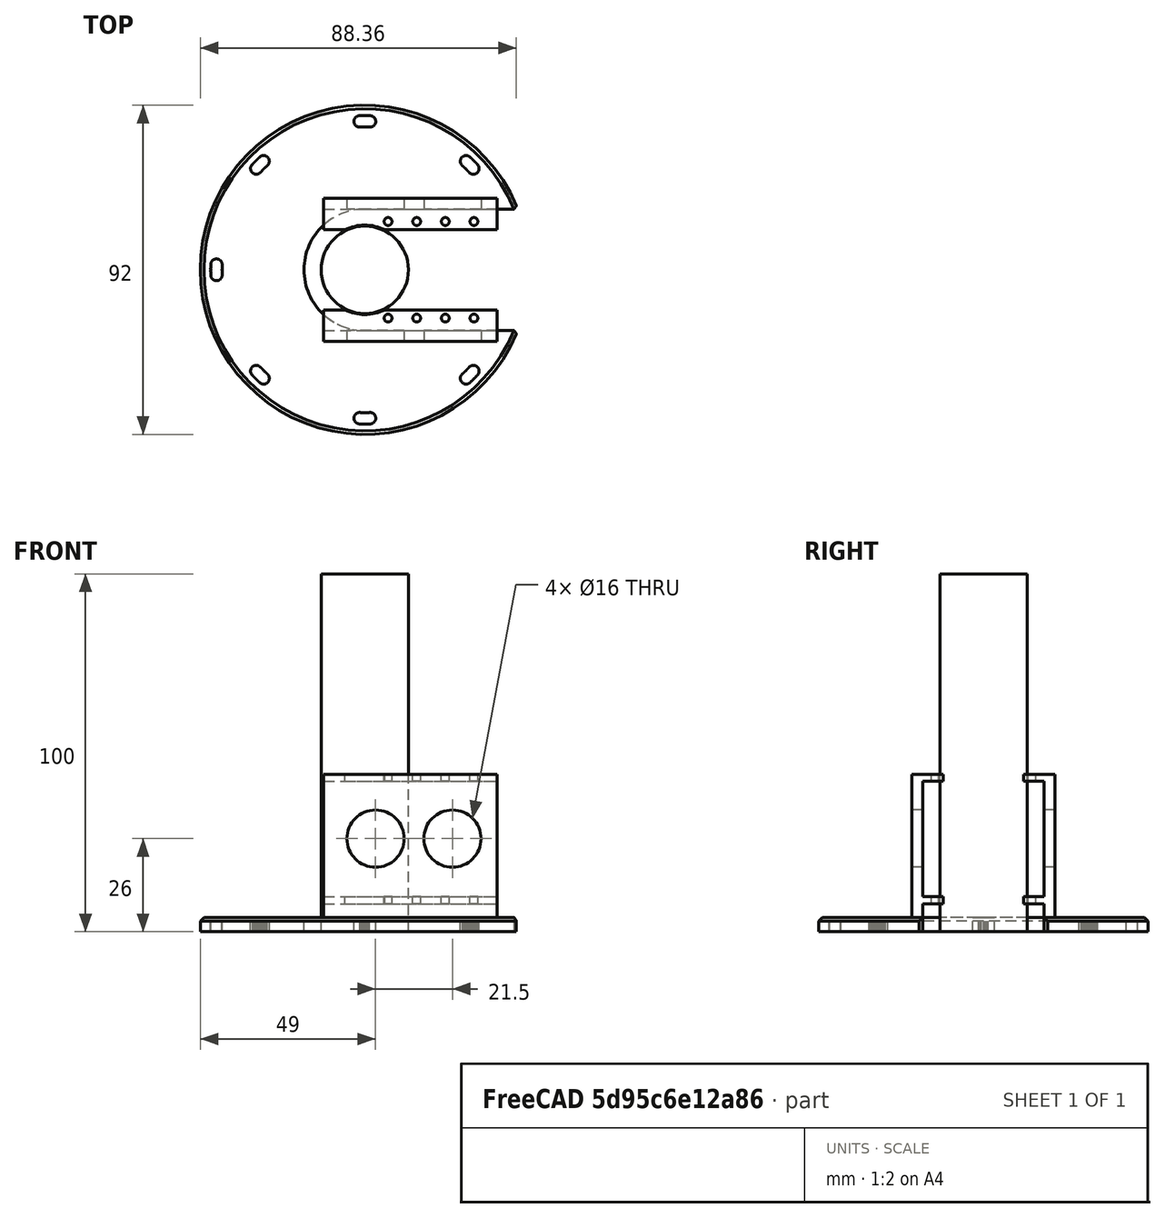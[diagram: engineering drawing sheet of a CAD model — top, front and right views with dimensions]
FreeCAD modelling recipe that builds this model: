
FCSTD DOCUMENT  (FreeCAD 0.15R4671 (Git))
Label: bottom_mount
License: All rights reserved
LicenseURL: http://en.wikipedia.org/wiki/All_rights_reserved
objects: Part::Cylinder×75, Part::MultiFuse×44, Part::Box×4, Part::Cut×3, Part::Chamfer×2, Part::Mirroring×1
note: 129 computed .brp shape members not serialized (recipe doc carries the construction recipe); baked Part::Feature solids carry a one-line shape summary decoded from their .brp

FEATURE [Part::Cylinder] Cylinder
  Angle = 360
  Height = 4
  Radius = 46
FEATURE [Part::Cylinder] Cylinder002
  Angle = 360
  Height = 10
  Radius = 17
FEATURE [Part::Box] Box001  label="Cube003"
  Height = 40
  Length = 48.5
  Placement = pos=(-13,-20,33) rot=(0,0,1;0rad)
  Width = 3
FEATURE [Part::Box] Box002  label="Cube004"
  Height = 2
  Length = 48.5
  Placement = pos=(-13,-17,71) rot=(0,0,1;0rad)
  Width = 5.8
FEATURE [Part::Box] Box003  label="Cube005"
  Height = 2
  Length = 48.5
  Placement = pos=(-13,-17,36.8) rot=(0,0,1;0rad)
  Width = 5.8
FEATURE [Part::Cylinder] Cylinder004 .. Cylinder007  x4 (patterned run collapsed; names and placements below)
  Angle = 360
  Height = 49
  Radius = 1.1
  placements: 4 in arithmetic series — first pos=(5,-13.5,28) rot=(0,0,1;0rad), step (8,0,0), last pos=(29,-13.5,28) rot=(0,0,1;0rad)
FEATURE [Part::MultiFuse] Fusion
  Shapes = -> [Box003,Box002,Box001]
FEATURE [Part::MultiFuse] Fusion001
  Shapes = -> [Cylinder007,Cylinder004,Cylinder006,Cylinder005]
FEATURE [Part::Cylinder] Cylinder012
  Angle = 360
  Height = 49
  Placement = pos=(-1.5,0,28) rot=(0,0,1;0rad)
  Radius = 12.5
FEATURE [Part::MultiFuse] Fusion002
  Shapes = -> [Fusion001,Cylinder012]
FEATURE [Part::Cut] Cut001
  Base = -> Fusion
  Placement = pos=(1.5,0,-29) rot=(0,0,1;0rad)
  Tool = -> Fusion002
FEATURE [Part::Box] Box  label="Cube"
  Height = 10
  Length = 100
  Placement = pos=(0,-17,0) rot=(0,0,1;0rad)
  Width = 34
FEATURE [Part::Cylinder] Cylinder013
  Angle = 360
  Height = 10
  Placement = pos=(23,0,0) rot=(0,0,1;0rad)
  Radius = 17
FEATURE [Part::MultiFuse] Fusion003
  Shapes = -> [Cylinder002,Box,Cylinder013]
FEATURE [Part::Cut] Cut
  Base = -> Cylinder
  Tool = -> Fusion003
FEATURE [Part::Mirroring] Part__Mirroring  label="Cut001 (Mirror #1)"
  Base = (0,0,0)
  Normal = (0,1,0)
  Source = -> Cut001
FEATURE [Part::Cylinder] Cylinder014
  Angle = 360
  Height = 10
  Placement = pos=(41.5,0,-2) rot=(0,0,1;0rad)
  Radius = 1.6
FEATURE [Part::Cylinder] Cylinder015
  Angle = 360
  Height = 10
  Placement = pos=(-41.5,0,-2) rot=(0,0,1;0rad)
  Radius = 1.6
FEATURE [Part::MultiFuse] Fusion004
  Placement = pos=(0,0,0) rot=(0,0,1;0.017453rad)
  Shapes = -> [Cylinder014,Cylinder015]
FEATURE [Part::Cylinder] Cylinder016
  Angle = 360
  Height = 10
  Placement = pos=(41.5,0,-2) rot=(0,0,1;0rad)
  Radius = 1.6
FEATURE [Part::Cylinder] Cylinder017
  Angle = 360
  Height = 10
  Placement = pos=(-41.5,0,-2) rot=(0,0,1;0rad)
  Radius = 1.6
FEATURE [Part::MultiFuse] Fusion005
  Placement = pos=(0,0,0) rot=(0,0,1;0.034907rad)
  Shapes = -> [Cylinder016,Cylinder017]
FEATURE [Part::Cylinder] Cylinder018
  Angle = 360
  Height = 10
  Placement = pos=(41.5,0,-2) rot=(0,0,1;0rad)
  Radius = 1.6
FEATURE [Part::Cylinder] Cylinder019
  Angle = 360
  Height = 10
  Placement = pos=(-41.5,0,-2) rot=(0,0,1;0rad)
  Radius = 1.6
FEATURE [Part::MultiFuse] Fusion006
  Placement = pos=(0,0,0) rot=(0,0,-1;0.017453rad)
  Shapes = -> [Cylinder018,Cylinder019]
FEATURE [Part::Cylinder] Cylinder020
  Angle = 360
  Height = 10
  Placement = pos=(41.5,0,-2) rot=(0,0,1;0rad)
  Radius = 1.6
FEATURE [Part::Cylinder] Cylinder021
  Angle = 360
  Height = 10
  Placement = pos=(-41.5,0,-2) rot=(0,0,1;0rad)
  Radius = 1.6
FEATURE [Part::MultiFuse] Fusion007
  Placement = pos=(0,0,0) rot=(0,0,-1;0.034907rad)
  Shapes = -> [Cylinder020,Cylinder021]
FEATURE [Part::Cylinder] Cylinder022
  Angle = 360
  Height = 10
  Placement = pos=(41.5,0,-2) rot=(0,0,1;0rad)
  Radius = 1.6
FEATURE [Part::Cylinder] Cylinder023
  Angle = 360
  Height = 10
  Placement = pos=(-41.5,0,-2) rot=(0,0,1;0rad)
  Radius = 1.6
FEATURE [Part::MultiFuse] Fusion008
  Placement = pos=(0,0,0) rot=(0,0,-1;0.008727rad)
  Shapes = -> [Cylinder022,Cylinder023]
FEATURE [Part::Cylinder] Cylinder024
  Angle = 360
  Height = 10
  Placement = pos=(41.5,0,-2) rot=(0,0,1;0rad)
  Radius = 1.6
FEATURE [Part::Cylinder] Cylinder025
  Angle = 360
  Height = 10
  Placement = pos=(-41.5,0,-2) rot=(0,0,1;0rad)
  Radius = 1.6
FEATURE [Part::MultiFuse] Fusion009
  Placement = pos=(0,0,0) rot=(0,0,-1;0.02618rad)
  Shapes = -> [Cylinder024,Cylinder025]
FEATURE [Part::Cylinder] Cylinder026
  Angle = 360
  Height = 10
  Placement = pos=(41.5,0,-2) rot=(0,0,1;0rad)
  Radius = 1.6
FEATURE [Part::Cylinder] Cylinder027
  Angle = 360
  Height = 10
  Placement = pos=(-41.5,0,-2) rot=(0,0,1;0rad)
  Radius = 1.6
FEATURE [Part::MultiFuse] Fusion010
  Placement = pos=(0,0,0) rot=(0,0,1;0.02618rad)
  Shapes = -> [Cylinder026,Cylinder027]
FEATURE [Part::Cylinder] Cylinder028
  Angle = 360
  Height = 10
  Placement = pos=(41.5,0,-2) rot=(0,0,1;0rad)
  Radius = 1.6
FEATURE [Part::Cylinder] Cylinder029
  Angle = 360
  Height = 10
  Placement = pos=(-41.5,0,-2) rot=(0,0,1;0rad)
  Radius = 1.6
FEATURE [Part::MultiFuse] Fusion011
  Placement = pos=(0,0,0) rot=(0,0,1;0.008727rad)
  Shapes = -> [Cylinder028,Cylinder029]
FEATURE [Part::MultiFuse] Fusion012
  Shapes = -> [Fusion007,Fusion010,Fusion005,Fusion009,Fusion006,Fusion008,Fusion004,Fusion011]
FEATURE [Part::MultiFuse] Fusion041
  Shapes = -> [Part__Mirroring,Cut001,Cut]
FEATURE [Part::Cylinder] Cylinder078
  Angle = 360
  Height = 100
  Placement = pos=(3,50,26) rot=(1,0,0;1.5708rad)
  Radius = 8
FEATURE [Part::Cylinder] Cylinder079
  Angle = 360
  Height = 100
  Placement = pos=(24.5,50,26) rot=(1,0,0;1.5708rad)
  Radius = 8
FEATURE [Part::MultiFuse] Fusion042
  Shapes = -> [Cylinder079,Cylinder078]
FEATURE [Part::Cylinder] Cylinder080
  Angle = 360
  Height = 10
  Placement = pos=(41.5,0,-2) rot=(0,0,1;0rad)
  Radius = 1.6
FEATURE [Part::Cylinder] Cylinder081
  Angle = 360
  Height = 10
  Placement = pos=(-41.5,0,-2) rot=(0,0,1;0rad)
  Radius = 1.6
FEATURE [Part::MultiFuse] Fusion043
  Placement = pos=(0,0,0) rot=(0,0,1;0.017453rad)
  Shapes = -> [Cylinder080,Cylinder081]
FEATURE [Part::Cylinder] Cylinder082
  Angle = 360
  Height = 10
  Placement = pos=(41.5,0,-2) rot=(0,0,1;0rad)
  Radius = 1.6
FEATURE [Part::Cylinder] Cylinder083
  Angle = 360
  Height = 10
  Placement = pos=(-41.5,0,-2) rot=(0,0,1;0rad)
  Radius = 1.6
FEATURE [Part::MultiFuse] Fusion044
  Placement = pos=(0,0,0) rot=(0,0,1;0.034907rad)
  Shapes = -> [Cylinder082,Cylinder083]
FEATURE [Part::Cylinder] Cylinder084
  Angle = 360
  Height = 10
  Placement = pos=(41.5,0,-2) rot=(0,0,1;0rad)
  Radius = 1.6
FEATURE [Part::Cylinder] Cylinder085
  Angle = 360
  Height = 10
  Placement = pos=(-41.5,0,-2) rot=(0,0,1;0rad)
  Radius = 1.6
FEATURE [Part::MultiFuse] Fusion045
  Placement = pos=(0,0,0) rot=(0,0,-1;0.017453rad)
  Shapes = -> [Cylinder084,Cylinder085]
FEATURE [Part::Cylinder] Cylinder086
  Angle = 360
  Height = 10
  Placement = pos=(41.5,0,-2) rot=(0,0,1;0rad)
  Radius = 1.6
FEATURE [Part::Cylinder] Cylinder087
  Angle = 360
  Height = 10
  Placement = pos=(-41.5,0,-2) rot=(0,0,1;0rad)
  Radius = 1.6
FEATURE [Part::MultiFuse] Fusion046
  Placement = pos=(0,0,0) rot=(0,0,-1;0.034907rad)
  Shapes = -> [Cylinder086,Cylinder087]
FEATURE [Part::Cylinder] Cylinder088
  Angle = 360
  Height = 10
  Placement = pos=(41.5,0,-2) rot=(0,0,1;0rad)
  Radius = 1.6
FEATURE [Part::Cylinder] Cylinder089
  Angle = 360
  Height = 10
  Placement = pos=(-41.5,0,-2) rot=(0,0,1;0rad)
  Radius = 1.6
FEATURE [Part::MultiFuse] Fusion047
  Placement = pos=(0,0,0) rot=(0,0,-1;0.008727rad)
  Shapes = -> [Cylinder088,Cylinder089]
FEATURE [Part::Cylinder] Cylinder090
  Angle = 360
  Height = 10
  Placement = pos=(41.5,0,-2) rot=(0,0,1;0rad)
  Radius = 1.6
FEATURE [Part::Cylinder] Cylinder091
  Angle = 360
  Height = 10
  Placement = pos=(-41.5,0,-2) rot=(0,0,1;0rad)
  Radius = 1.6
FEATURE [Part::MultiFuse] Fusion048
  Placement = pos=(0,0,0) rot=(0,0,-1;0.02618rad)
  Shapes = -> [Cylinder090,Cylinder091]
FEATURE [Part::Cylinder] Cylinder092
  Angle = 360
  Height = 10
  Placement = pos=(41.5,0,-2) rot=(0,0,1;0rad)
  Radius = 1.6
FEATURE [Part::Cylinder] Cylinder093
  Angle = 360
  Height = 10
  Placement = pos=(-41.5,0,-2) rot=(0,0,1;0rad)
  Radius = 1.6
FEATURE [Part::MultiFuse] Fusion049
  Placement = pos=(0,0,0) rot=(0,0,1;0.02618rad)
  Shapes = -> [Cylinder092,Cylinder093]
FEATURE [Part::Cylinder] Cylinder094
  Angle = 360
  Height = 10
  Placement = pos=(41.5,0,-2) rot=(0,0,1;0rad)
  Radius = 1.6
FEATURE [Part::Cylinder] Cylinder095
  Angle = 360
  Height = 10
  Placement = pos=(-41.5,0,-2) rot=(0,0,1;0rad)
  Radius = 1.6
FEATURE [Part::MultiFuse] Fusion050
  Placement = pos=(0,0,0) rot=(0,0,1;0.008727rad)
  Shapes = -> [Cylinder094,Cylinder095]
FEATURE [Part::MultiFuse] Fusion051
  Placement = pos=(0,0,0) rot=(0,0,1;0.785398rad)
  Shapes = -> [Fusion046,Fusion049,Fusion044,Fusion048,Fusion045,Fusion047,Fusion043,Fusion050]
FEATURE [Part::Cylinder] Cylinder096
  Angle = 360
  Height = 10
  Placement = pos=(41.5,0,-2) rot=(0,0,1;0rad)
  Radius = 1.6
FEATURE [Part::Cylinder] Cylinder097
  Angle = 360
  Height = 10
  Placement = pos=(-41.5,0,-2) rot=(0,0,1;0rad)
  Radius = 1.6
FEATURE [Part::MultiFuse] Fusion052
  Placement = pos=(0,0,0) rot=(0,0,1;0.017453rad)
  Shapes = -> [Cylinder096,Cylinder097]
FEATURE [Part::Cylinder] Cylinder098
  Angle = 360
  Height = 10
  Placement = pos=(41.5,0,-2) rot=(0,0,1;0rad)
  Radius = 1.6
FEATURE [Part::Cylinder] Cylinder099
  Angle = 360
  Height = 10
  Placement = pos=(-41.5,0,-2) rot=(0,0,1;0rad)
  Radius = 1.6
FEATURE [Part::MultiFuse] Fusion053
  Placement = pos=(0,0,0) rot=(0,0,1;0.034907rad)
  Shapes = -> [Cylinder098,Cylinder099]
FEATURE [Part::Cylinder] Cylinder100
  Angle = 360
  Height = 10
  Placement = pos=(41.5,0,-2) rot=(0,0,1;0rad)
  Radius = 1.6
FEATURE [Part::Cylinder] Cylinder101
  Angle = 360
  Height = 10
  Placement = pos=(-41.5,0,-2) rot=(0,0,1;0rad)
  Radius = 1.6
FEATURE [Part::MultiFuse] Fusion054
  Placement = pos=(0,0,0) rot=(0,0,-1;0.017453rad)
  Shapes = -> [Cylinder100,Cylinder101]
FEATURE [Part::Cylinder] Cylinder102
  Angle = 360
  Height = 10
  Placement = pos=(41.5,0,-2) rot=(0,0,1;0rad)
  Radius = 1.6
FEATURE [Part::Cylinder] Cylinder103
  Angle = 360
  Height = 10
  Placement = pos=(-41.5,0,-2) rot=(0,0,1;0rad)
  Radius = 1.6
FEATURE [Part::MultiFuse] Fusion055
  Placement = pos=(0,0,0) rot=(0,0,-1;0.034907rad)
  Shapes = -> [Cylinder102,Cylinder103]
FEATURE [Part::Cylinder] Cylinder104
  Angle = 360
  Height = 10
  Placement = pos=(41.5,0,-2) rot=(0,0,1;0rad)
  Radius = 1.6
FEATURE [Part::Cylinder] Cylinder105
  Angle = 360
  Height = 10
  Placement = pos=(-41.5,0,-2) rot=(0,0,1;0rad)
  Radius = 1.6
FEATURE [Part::MultiFuse] Fusion056
  Placement = pos=(0,0,0) rot=(0,0,-1;0.008727rad)
  Shapes = -> [Cylinder104,Cylinder105]
FEATURE [Part::Cylinder] Cylinder106
  Angle = 360
  Height = 10
  Placement = pos=(41.5,0,-2) rot=(0,0,1;0rad)
  Radius = 1.6
FEATURE [Part::Cylinder] Cylinder107
  Angle = 360
  Height = 10
  Placement = pos=(-41.5,0,-2) rot=(0,0,1;0rad)
  Radius = 1.6
FEATURE [Part::MultiFuse] Fusion057
  Placement = pos=(0,0,0) rot=(0,0,-1;0.02618rad)
  Shapes = -> [Cylinder106,Cylinder107]
FEATURE [Part::Cylinder] Cylinder108
  Angle = 360
  Height = 10
  Placement = pos=(41.5,0,-2) rot=(0,0,1;0rad)
  Radius = 1.6
FEATURE [Part::Cylinder] Cylinder109
  Angle = 360
  Height = 10
  Placement = pos=(-41.5,0,-2) rot=(0,0,1;0rad)
  Radius = 1.6
FEATURE [Part::MultiFuse] Fusion058
  Placement = pos=(0,0,0) rot=(0,0,1;0.02618rad)
  Shapes = -> [Cylinder108,Cylinder109]
FEATURE [Part::Cylinder] Cylinder110
  Angle = 360
  Height = 10
  Placement = pos=(41.5,0,-2) rot=(0,0,1;0rad)
  Radius = 1.6
FEATURE [Part::Cylinder] Cylinder111
  Angle = 360
  Height = 10
  Placement = pos=(-41.5,0,-2) rot=(0,0,1;0rad)
  Radius = 1.6
FEATURE [Part::MultiFuse] Fusion059
  Placement = pos=(0,0,0) rot=(0,0,1;0.008727rad)
  Shapes = -> [Cylinder110,Cylinder111]
FEATURE [Part::MultiFuse] Fusion060
  Placement = pos=(0,0,0) rot=(0,0,-1;0.785398rad)
  Shapes = -> [Fusion055,Fusion058,Fusion053,Fusion057,Fusion054,Fusion056,Fusion052,Fusion059]
FEATURE [Part::Cylinder] Cylinder112
  Angle = 360
  Height = 10
  Placement = pos=(41.5,0,-2) rot=(0,0,1;0rad)
  Radius = 1.6
FEATURE [Part::Cylinder] Cylinder113
  Angle = 360
  Height = 10
  Placement = pos=(-41.5,0,-2) rot=(0,0,1;0rad)
  Radius = 1.6
FEATURE [Part::MultiFuse] Fusion061
  Placement = pos=(0,0,0) rot=(0,0,1;0.017453rad)
  Shapes = -> [Cylinder112,Cylinder113]
FEATURE [Part::Cylinder] Cylinder114
  Angle = 360
  Height = 10
  Placement = pos=(41.5,0,-2) rot=(0,0,1;0rad)
  Radius = 1.6
FEATURE [Part::Cylinder] Cylinder115
  Angle = 360
  Height = 10
  Placement = pos=(-41.5,0,-2) rot=(0,0,1;0rad)
  Radius = 1.6
FEATURE [Part::MultiFuse] Fusion062
  Placement = pos=(0,0,0) rot=(0,0,1;0.034907rad)
  Shapes = -> [Cylinder114,Cylinder115]
FEATURE [Part::Cylinder] Cylinder116
  Angle = 360
  Height = 10
  Placement = pos=(41.5,0,-2) rot=(0,0,1;0rad)
  Radius = 1.6
FEATURE [Part::Cylinder] Cylinder117
  Angle = 360
  Height = 10
  Placement = pos=(-41.5,0,-2) rot=(0,0,1;0rad)
  Radius = 1.6
FEATURE [Part::MultiFuse] Fusion063
  Placement = pos=(0,0,0) rot=(0,0,-1;0.017453rad)
  Shapes = -> [Cylinder116,Cylinder117]
FEATURE [Part::Cylinder] Cylinder118
  Angle = 360
  Height = 10
  Placement = pos=(41.5,0,-2) rot=(0,0,1;0rad)
  Radius = 1.6
FEATURE [Part::Cylinder] Cylinder119
  Angle = 360
  Height = 10
  Placement = pos=(-41.5,0,-2) rot=(0,0,1;0rad)
  Radius = 1.6
FEATURE [Part::MultiFuse] Fusion064
  Placement = pos=(0,0,0) rot=(0,0,-1;0.034907rad)
  Shapes = -> [Cylinder118,Cylinder119]
FEATURE [Part::Cylinder] Cylinder120
  Angle = 360
  Height = 10
  Placement = pos=(41.5,0,-2) rot=(0,0,1;0rad)
  Radius = 1.6
FEATURE [Part::Cylinder] Cylinder121
  Angle = 360
  Height = 10
  Placement = pos=(-41.5,0,-2) rot=(0,0,1;0rad)
  Radius = 1.6
FEATURE [Part::MultiFuse] Fusion065
  Placement = pos=(0,0,0) rot=(0,0,-1;0.008727rad)
  Shapes = -> [Cylinder120,Cylinder121]
FEATURE [Part::Cylinder] Cylinder122
  Angle = 360
  Height = 10
  Placement = pos=(41.5,0,-2) rot=(0,0,1;0rad)
  Radius = 1.6
FEATURE [Part::Cylinder] Cylinder123
  Angle = 360
  Height = 10
  Placement = pos=(-41.5,0,-2) rot=(0,0,1;0rad)
  Radius = 1.6
FEATURE [Part::MultiFuse] Fusion066
  Placement = pos=(0,0,0) rot=(0,0,-1;0.02618rad)
  Shapes = -> [Cylinder122,Cylinder123]
FEATURE [Part::Cylinder] Cylinder124
  Angle = 360
  Height = 10
  Placement = pos=(41.5,0,-2) rot=(0,0,1;0rad)
  Radius = 1.6
FEATURE [Part::Cylinder] Cylinder125
  Angle = 360
  Height = 10
  Placement = pos=(-41.5,0,-2) rot=(0,0,1;0rad)
  Radius = 1.6
FEATURE [Part::MultiFuse] Fusion067
  Placement = pos=(0,0,0) rot=(0,0,1;0.02618rad)
  Shapes = -> [Cylinder124,Cylinder125]
FEATURE [Part::Cylinder] Cylinder126
  Angle = 360
  Height = 10
  Placement = pos=(41.5,0,-2) rot=(0,0,1;0rad)
  Radius = 1.6
FEATURE [Part::Cylinder] Cylinder127
  Angle = 360
  Height = 10
  Placement = pos=(-41.5,0,-2) rot=(0,0,1;0rad)
  Radius = 1.6
FEATURE [Part::MultiFuse] Fusion068
  Placement = pos=(0,0,0) rot=(0,0,1;0.008727rad)
  Shapes = -> [Cylinder126,Cylinder127]
FEATURE [Part::MultiFuse] Fusion069
  Placement = pos=(0,0,0) rot=(0,0,1;1.5708rad)
  Shapes = -> [Fusion064,Fusion067,Fusion062,Fusion066,Fusion063,Fusion065,Fusion061,Fusion068]
FEATURE [Part::MultiFuse] Fusion070
  Shapes = -> [Fusion069,Fusion060,Fusion012,Fusion051]
FEATURE [Part::Cylinder] Cylinder128
  Angle = 360
  Height = 100
  Radius = 12.2
FEATURE [Part::MultiFuse] Fusion071
  Shapes = -> [Fusion042,Fusion070]
FEATURE [Part::Chamfer] Chamfer
  Base = -> Fusion041
  Edges = 1 edges r=1: [Edge35]
FEATURE [Part::Chamfer] Chamfer001
  Base = -> Chamfer
  Edges = 2 edges r=1: [Edge13,Edge26]
FEATURE [Part::Cut] Cut002
  Base = -> Chamfer001
  Tool = -> Fusion071
